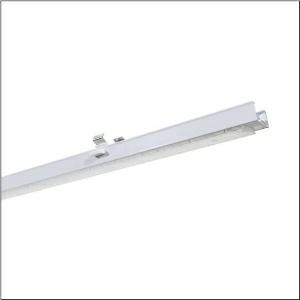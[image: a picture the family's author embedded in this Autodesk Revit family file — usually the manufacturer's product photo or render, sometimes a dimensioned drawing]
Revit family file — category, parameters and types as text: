
# Revit family: trunking_flex_31_51re12mb48b
name_source: partatom
category: Lighting Fixtures
units: mm (PartAtom-declared; Revit-internal decimal feet)

## family parameters
Cut with Voids When Loaded = No
Host = Face
Light Source = No
Part Type = Normal
Room Calculation Point = No
Round Connector Dimension = Use Diameter
Shared = No

## types (1)
- --- (1 x LED, 8000 lm, 50 W, 4000K)
    Apparent Load = 50 VA
    CIE Flux Codes = 65 91 98 99 100
    Color Rendering = 80
    Color Temperature = 4000K
    Default Elevation = 1800 mm
    Description = Trunking Flex 31, luminaire insert, of extruded aluminium section, coated, traffic white (RAL 9016), length: 1.472mm, width: 91mm, height: 53mm, LED rated luminous flux: 8.000lm, light colour: 840, control gear: ON/OFF Multilumen, with system connector: socket, mains connection: 220..240V, AC, 50/60Hz, rated input power: 50W, luminous flux adjustable on luminaire in four steps (4130/5610/6850/8000lm), connected load according to luminous flux setting (25/34/42/50W), primary light control with lens, of plastic, primary optical cover: cover, of PMMA, light emission: direct distribution, protection rating (complete): IP20, insulation class (complete): insulation class I (protective earthing), certification: CE, UKCA, impact resistance: IK02, permissible ambient temperature for indoor applications: -20..+40°C, packaging unit: 1 piece
    Height = 58 mm
    Lamp = 1 x LED
    Lamp Light Flux = 8000 lm
    Lamp Power = 50 W
    Lamp count = 1
    Length = 1472 mm
    Luminous efficacy = 160 lm/W
    Manufacturer = Siteco
    ModVariant = No
    Model = 51RE12MB48B
    Mounting Place = Ceiling
    Mounting Type = Pendant
    Number of Poles = 1
    OnlyDefault = Yes
    Power Factor = 1
    Product Name = Trunking Flex 31
    Product group = luminaire insert
    ProductGroupID = 902
    Protection Class = Protection class I
    Protection Degree = IP 20
    RLX_Detail_Level = 1
    RLX_Emergency_Light_Flux = 0 lm
    RLX_Emergency_Type = 0
    RLX_Emergency_Type_DB = No
    RlxData = <blob elided: 20341 chars, md5=4453be4f>
    Socket = socket
    Standby Power = 0 W
    System Light Flux = 8000 lm
    System Power = 50 W
    Type Comments = factory setting: luminous flux: 100 % | (ON | ON) | 300 mA
    Type Image = l_1266702.jpg
    URL = http://relux.com
    VarID = @adj_059166
    Voltage = 0 V
    Weight = 0.00 kg
    Width = 65 mm

## geometry (parser evidence)
native form markers: Blend x4, Sweep x11
no freeform markers — native parametric forms only
